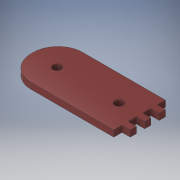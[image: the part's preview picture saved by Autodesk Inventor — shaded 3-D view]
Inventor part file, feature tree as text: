
AUTODESK INVENTOR PART (.ipt)
format: ipt  version: 2019.1 (Build 231200000, 200)  size: 147,456 bytes
history: native  units: in
note: dims shown in document units (in); Inventor stores cm internally (conversion verified against a paired STEP export)
features: extrude x2, sketch x2
ambient origin geometry x8: Origin, YZ Plane, XZ Plane, XY Plane, X Axis, Y Axis, Z Axis, Center Point
bodies: Body1 (feature_tree)
feature tree (4):
  extrude  "Extrusion7"  Depth=0.0787in
  extrude  "Extrusion8"  Depth=0.0787in
  sketch  "Sketch1"  dims[d2=0.2362in d5=0.0787in]
  sketch  "Sketch2"  dims[d15=0.0in d26=0.0787in d27=0.0787in d28=0.0787in d29=0.0787in d30=0.0787in d31=0.0787in d32=0.0591in d33=0.0591in d34=0.0787in d35=0.0591in d36=0.0787in d37=0.06in d38=0.0in d39=0.7874in d40=0.0787in d43=0.5906in d44=0.2461in d45=0.3937in d46=0.0in]
